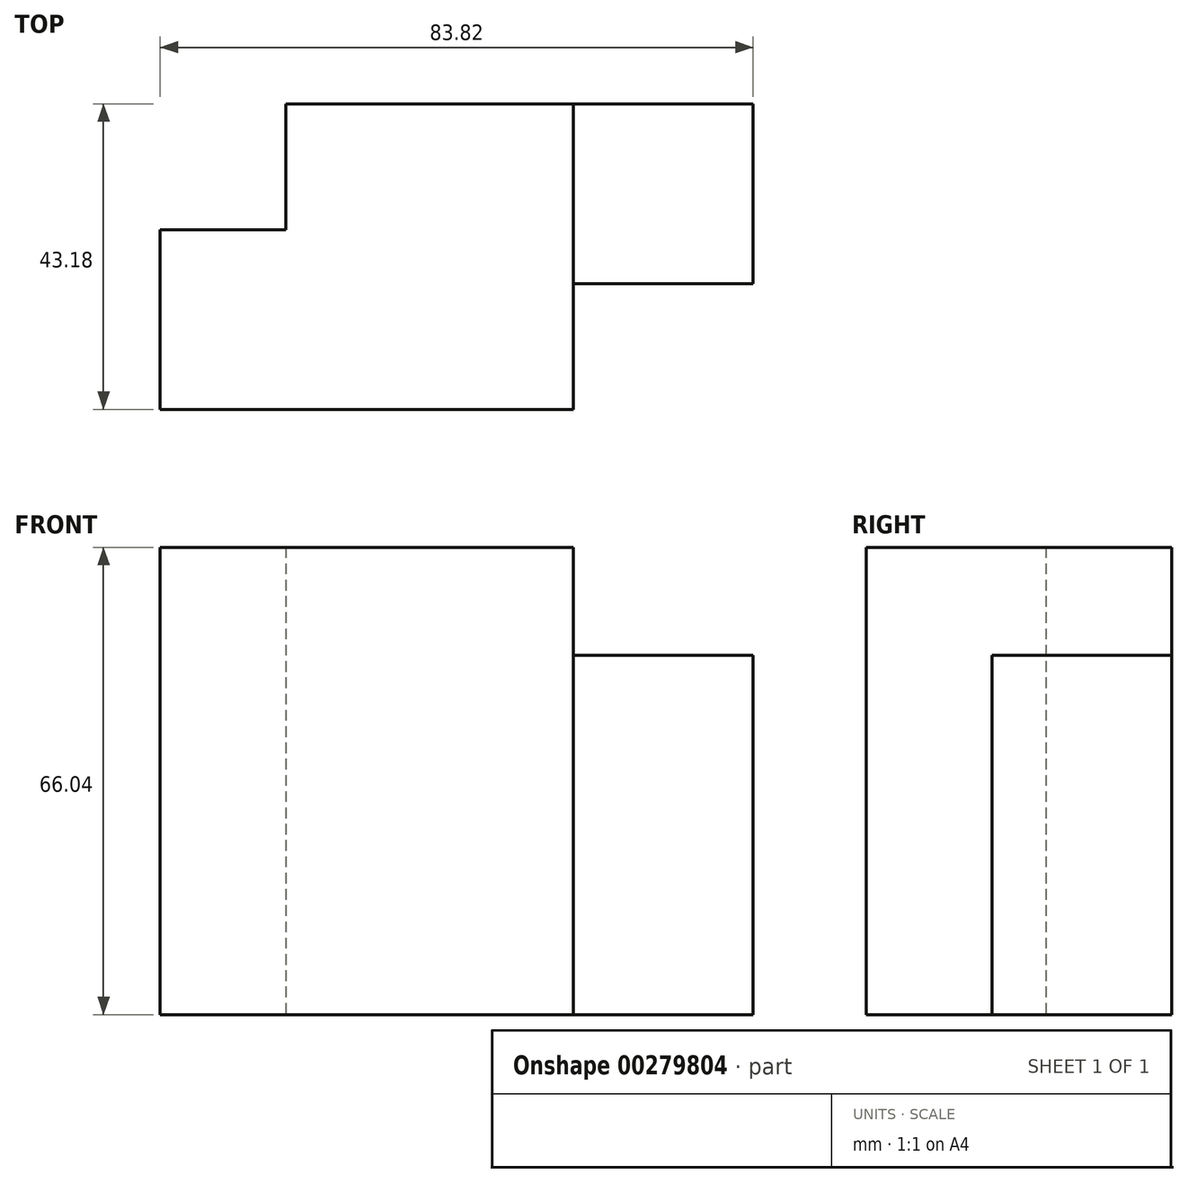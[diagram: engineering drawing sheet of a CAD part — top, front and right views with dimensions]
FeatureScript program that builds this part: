
annotation { "Feature Type Name" : "Feature", "Feature Type Description" : "" }
export const myFeature = defineFeature(function(context is Context, id is Id, definition is map)
    precondition{}
    {
        {
            var Q0;
            Q0=qCreatedBy(makeId("Front.planeOp"),FACE);
            var sketch = newSketch(context, id + "F0", { "sketchPlane" : qUnion([Q0])});
            skLineSegment(sketch, "E0.bottom", {"start": v(-14.08, 11.25) * mm, "end": v(-80.12, 11.25) * mm});
            skLineSegment(sketch, "E0.top", {"start": v(-14.08, -39.55) * mm, "end": v(-80.12, -39.55) * mm});
            skLineSegment(sketch, "E0.left", {"start": v(-14.08, 11.25) * mm, "end": v(-14.08, -39.55) * mm});
            skLineSegment(sketch, "E0.right", {"start": v(-80.12, 11.25) * mm, "end": v(-80.12, -39.55) * mm});
            skSolve(sketch);
        }
        {
            var Q0;
            Q0=makeQuery(id+"F0.imprint","IMPRINT",FACE,{"disambiguationData":[TD([[makeQuery(id+"F0.imprint","IMPRINT",EDGE,{"derivedFrom":sQuery(id+"F0.wireOp",EDGE,"E0.bottom")}),1.0]])]});
            extrude(context, id + "F1", {"entities" : qUnion([Q0]), "oppositeDirection" : true, "depth" : 25.4 * mm});
        }
        {
            var Q0;
            Q0=makeQuery(id+"F1.opExtrude","CAP_FACE",FACE,{"disambiguationData":[OSD([sQuery(id+"F0.wireOp",EDGE,"E0.bottom"),sQuery(id+"F0.wireOp",EDGE,"E0.top"),sQuery(id+"F0.wireOp",EDGE,"E0.left"),sQuery(id+"F0.wireOp",EDGE,"E0.right")])],"isStart":true});
            var sketch = newSketch(context, id + "F2", { "sketchPlane" : qUnion([Q0])});
            skLineSegment(sketch, "E1", {"start": v(-39.48, 11.25) * mm, "end": v(-39.48, -39.55) * mm});
            skLineSegment(sketch, "E2", {"start": v(-80.12, -14.15) * mm, "end": v(-14.08, -14.15) * mm});
            skSolve(sketch);
        }
        {
            var Q0;
            {var subQ0=sQuery(id+"F2.wireOp",EDGE,"E1");var subQ1=makeQuery(id+"F1.opExtrude","CAP_EDGE",EDGE,{"disambiguationData":[OSD([sQuery(id+"F0.wireOp",EDGE,"E0.bottom")])],"isStart":true});var subQ2=makeQuery(id+"F2.imprint","INTERSECT",VERTEX,{"derivedFrom":[subQ1,subQ0]});Q0=makeQuery(id+"F2.imprint","IMPRINT",FACE,{"disambiguationData":[TD([[makeQuery(id+"F2.imprint","IMPRINT",EDGE,{"disambiguationData":[TD([[subQ2,-1.0]])],"derivedFrom":subQ0}),-1.0]])]});}
            var Q1;
            {var subQ0=sQuery(id+"F2.wireOp",EDGE,"E1");var subQ1=makeQuery(id+"F1.opExtrude","CAP_EDGE",EDGE,{"disambiguationData":[OSD([sQuery(id+"F0.wireOp",EDGE,"E0.top")])],"isStart":true});var subQ2=makeQuery(id+"F2.imprint","INTERSECT",VERTEX,{"derivedFrom":[subQ1,subQ0]});Q1=makeQuery(id+"F2.imprint","IMPRINT",FACE,{"disambiguationData":[TD([[makeQuery(id+"F2.imprint","IMPRINT",EDGE,{"disambiguationData":[TD([[subQ2,1.0]])],"derivedFrom":subQ0}),-1.0]])]});}
            var Q2;
            {var subQ0=sQuery(id+"F2.wireOp",EDGE,"E1");var subQ1=makeQuery(id+"F1.opExtrude","CAP_EDGE",EDGE,{"disambiguationData":[OSD([sQuery(id+"F0.wireOp",EDGE,"E0.bottom")])],"isStart":true});var subQ2=makeQuery(id+"F2.imprint","INTERSECT",VERTEX,{"derivedFrom":[subQ1,subQ0]});Q2=makeQuery(id+"F2.imprint","IMPRINT",FACE,{"disambiguationData":[TD([[makeQuery(id+"F2.imprint","IMPRINT",EDGE,{"disambiguationData":[TD([[subQ2,-1.0]])],"derivedFrom":subQ0}),1.0]])]});}
            extrude(context, id + "F3", {"entities" : qUnion([Q0, Q1, Q2]), "operationType" : NewBodyOperationType.ADD, "depth" : 17.78 * mm});
        }
        {
            var Q0;
            {var subQ0=sQuery(id+"F0.wireOp",EDGE,"E0.bottom");Q0=makeQuery(id+"F3.boolean.opBoolean","MERGE",FACE,{"derivedFrom":[makeQuery(id+"F1.opExtrude","SWEPT_FACE",FACE,{"disambiguationData":[OSD([subQ0])]}),makeQuery(id+"F3.opExtrude","SWEPT_FACE",FACE,{"disambiguationData":[OSD([subQ0])]})]});}
            var sketch = newSketch(context, id + "F4", { "sketchPlane" : qUnion([Q0])});
            skLineSegment(sketch, "E3", {"start": v(-39.48, 25.4) * mm, "end": v(-39.48, -17.78) * mm});
            skSolve(sketch);
        }
        {
            var Q0;
            {var subQ0=sQuery(id+"F4.wireOp",EDGE,"E3");Q0=makeQuery(id+"F4.imprint","IMPRINT",FACE,{"disambiguationData":[TD([[makeQuery(id+"F4.imprint","IMPRINT",EDGE,{"derivedFrom":subQ0}),-1.0]])]});}
            extrude(context, id + "F5", {"entities" : qUnion([Q0]), "operationType" : NewBodyOperationType.ADD, "depth" : 15.24 * mm});
        }
        {
            var Q0;
            {var subQ0=sQuery(id+"F0.wireOp",EDGE,"E0.right");var subQ1=sQuery(id+"F0.wireOp",EDGE,"E0.bottom");var subQ2=makeQuery(id+"F3.opExtrude","CAP_EDGE",EDGE,{"disambiguationData":[OSD([subQ1])],"isStart":false});Q0=makeQuery(id+"F5.boolean.opBoolean","MERGE",FACE,{"derivedFrom":[makeQuery(id+"F3.opExtrude","CAP_FACE",FACE,{"disambiguationData":[OSD([subQ1,sQuery(id+"F0.wireOp",EDGE,"E0.top"),sQuery(id+"F0.wireOp",EDGE,"E0.left"),subQ0,sQuery(id+"F2.wireOp",EDGE,"E1"),sQuery(id+"F2.wireOp",EDGE,"E2")])],"isStart":false}),makeQuery(id+"F5.opExtrude","SWEPT_FACE",FACE,{"disambiguationData":[OSD([subQ1]),TDD([makeQuery(id+"F4.imprint","IMPRINT",EDGE,{"disambiguationData":[TD([[makeQuery(id+"F4.imprint","INTERSECT",VERTEX,{"derivedFrom":[subQ2,sQuery(id+"F4.wireOp",EDGE,"E3")]}),-1.0]])],"derivedFrom":subQ2})])]})]});}
            var sketch = newSketch(context, id + "F6", { "sketchPlane" : qUnion([Q0])});
            skLineSegment(sketch, "E4", {"start": v(-39.48, 11.25) * mm, "end": v(-39.48, -14.15) * mm});
            skSolve(sketch);
        }
        {
            var Q0;
            Q0=makeQuery(id+"F6.imprint","IMPRINT",FACE,{"disambiguationData":[TD([[makeQuery(id+"F6.imprint","IMPRINT",EDGE,{"derivedFrom":sQuery(id+"F6.wireOp",EDGE,"E4")}),1.0]])]});
            extrude(context, id + "F7", {"entities" : qUnion([Q0]), "operationType" : NewBodyOperationType.REMOVE, "oppositeDirection" : true, "depth" : 17.78 * mm});
        }
        {
            var Q0;
            {var subQ0=sQuery(id+"F0.wireOp",EDGE,"E0.right");Q0=makeQuery(id+"F5.boolean.opBoolean","MERGE",FACE,{"derivedFrom":[makeQuery(id+"F3.boolean.opBoolean","MERGE",FACE,{"derivedFrom":[makeQuery(id+"F1.opExtrude","SWEPT_FACE",FACE,{"disambiguationData":[OSD([subQ0])]}),makeQuery(id+"F3.opExtrude","SWEPT_FACE",FACE,{"disambiguationData":[OSD([subQ0])]})]}),makeQuery(id+"F5.opExtrude","SWEPT_FACE",FACE,{"disambiguationData":[OSD([sQuery(id+"F0.wireOp",EDGE,"E0.bottom"),subQ0])]})]});}
            var sketch = newSketch(context, id + "F8", { "sketchPlane" : qUnion([Q0])});
            skLineSegment(sketch, "E5", {"start": v(-7.62, 26.5) * mm, "end": v(-7.62, -39.55) * mm});
            skSolve(sketch);
        }
        {
            var Q0;
            Q0 = qSketchRegion(id + "F8", true);
            var Q1;
            {var subQ0=sQuery(id+"F8.wireOp",EDGE,"E5");Q1=makeQuery(id+"F8.imprint","IMPRINT",FACE,{"disambiguationData":[TD([[makeQuery(id+"F8.imprint","IMPRINT",EDGE,{"derivedFrom":subQ0}),1.0]])]});}
            extrude(context, id + "F9", {"entities" : qUnion([Q0, Q1]), "operationType" : NewBodyOperationType.ADD, "depth" : 17.78 * mm});
        }
    });
